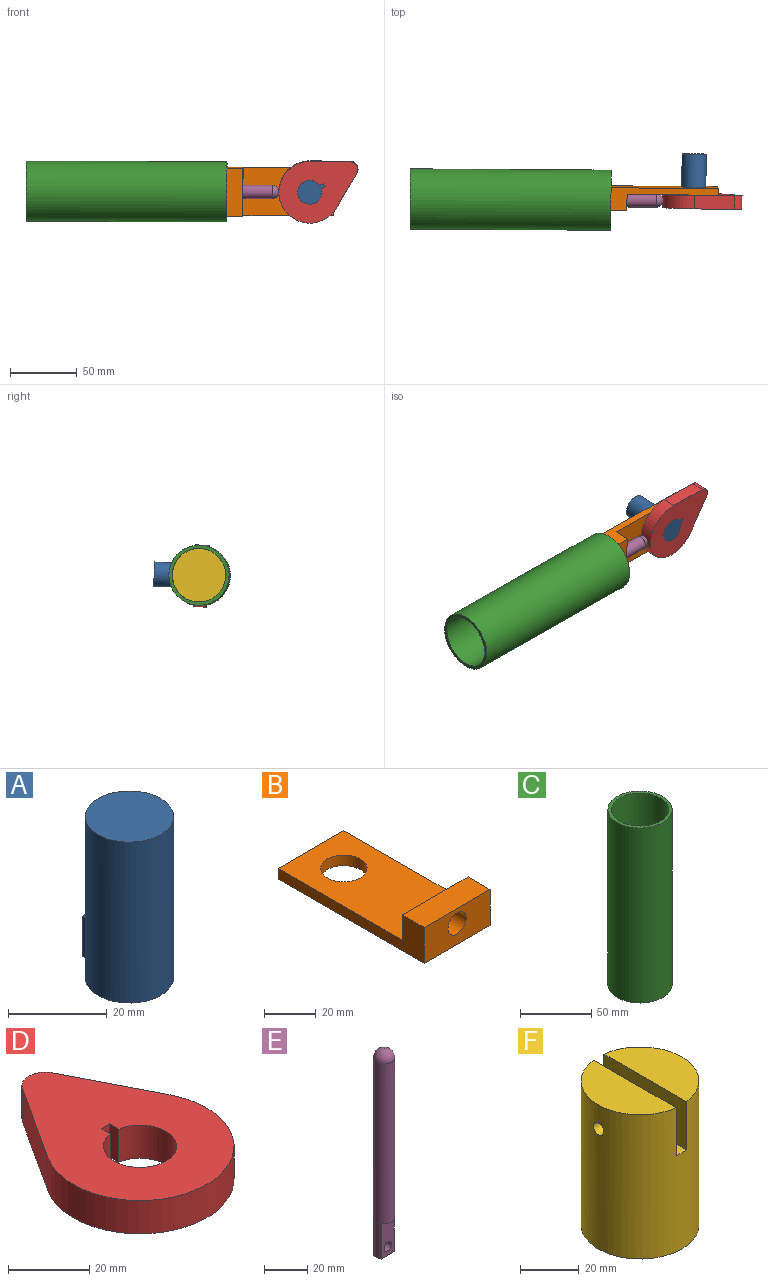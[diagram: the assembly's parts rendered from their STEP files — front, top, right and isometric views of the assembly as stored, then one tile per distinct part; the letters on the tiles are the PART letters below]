
ASSEMBLY  parts=6 mates=7
PART A: 7 faces, bbox 18x21x40 mm
  f0: plane 10x3.13mm, normal (-1,0,0), area 31.3mm2, adj f2,f4,f5,f6
  f1: plane 10x3.13mm, normal (1,0,0), area 31.3mm2, adj f2,f4,f5,f6
  f2: plane 10x3mm, normal (0,1,0), area 30mm2, adj f0,f1,f5,f6
  f3: plane 18x18mm, normal (0,0,1), area 254.5mm2, adj f4
  f4: cylinder r=9mm len=40mm, axis (0,0,-1), area 2231.8mm2, adj f0,f1,f3,f5,f6
  f5: plane 21x18mm, normal (0,0,-1), area 263.6mm2, adj f0,f1,f2,f4
  f6: plane 3.13x3mm, normal (0,0,1), area 9.1mm2, adj f0,f1,f2,f4
PART B: 10 faces, bbox 36x80x17 mm
  f0: plane 68x36mm, normal (0,0,1), area 2193.5mm2, adj f1,f3,f4,f5,f7
  f1: plane 80x17mm, normal (-1,0,0), area 544mm2, adj f0,f2,f4,f6,f7,f8
  f2: plane 36x17mm, normal (0,-1,0), area 533.5mm2, adj f1,f3,f6,f8,f9
  f3: plane 80x17mm, normal (1,0,0), area 544mm2, adj f0,f2,f4,f6,f7,f8
  f4: plane 36x5mm, normal (0,1,0), area 180mm2, adj f0,f1,f3,f6
  f5: cylinder r=9mm len=18mm, axis (0,0,-1), area 282.7mm2, adj f0,f6
  f6: plane 80x36mm, normal (0,0,-1), area 2625.5mm2, adj f1,f2,f3,f4,f5
  f7: plane 36x12mm, normal (0,1,0), area 353.5mm2, adj f0,f1,f3,f8,f9
  f8: plane 36x12mm, normal (0,0,1), area 432mm2, adj f1,f2,f3,f7
  f9: cylinder r=5mm len=12mm, axis (0,1,0), area 377mm2, adj f2,f7
PART C: 4 faces, bbox 45x45x150 mm
  f0: cylinder r=20mm len=150mm, axis (0,0,-1), area 18849.6mm2, adj f2,f3
  f1: cylinder r=22.5mm len=150mm, axis (0,0,-1), area 21205.8mm2, adj f2,f3
  f2: plane 45x45mm, normal (0,0,1), area 333.8mm2, adj f0,f1
  f3: plane 45x45mm, normal (0,0,-1), area 333.8mm2, adj f0,f1
PART D: 10 faces, bbox 46.2x63.5x10 mm
  f0: cylinder r=9mm len=18mm, axis (0,0,-1), area 535.3mm2, adj f1,f2,f7,f9
  f1: plane 63.48x46.2mm, normal (0,0,1), area 1755.7mm2, adj f0,f3,f4,f5,f6,f7,f8,f9
  f2: plane 63.48x46.2mm, normal (0,0,-1), area 1755.7mm2, adj f0,f3,f4,f5,f6,f7,f8,f9
  f3: cylinder r=5.78mm len=10mm, axis (0,0,-1), area 121.1mm2, adj f1,f2,f4,f6
  f4: plane 25.16x16.33mm, normal (-0.84,0.54,0), area 300mm2, adj f1,f2,f3,f5
  f5: cylinder r=23.1mm len=46.2mm, axis (0,0,-1), area 967.7mm2, adj f1,f2,f4,f6
  f6: plane 26.73x13.63mm, normal (0.89,0.45,0), area 300mm2, adj f1,f2,f3,f5
  f7: plane 10x3.13mm, normal (-1,0,0), area 31.3mm2, adj f0,f1,f2,f8
  f8: plane 10x3mm, normal (0,-1,0), area 30mm2, adj f1,f2,f7,f9
  f9: plane 10x3.13mm, normal (1,0,0), area 31.3mm2, adj f0,f1,f2,f8
PART E: 8 faces, bbox 10x10x115 mm
  f0: plane 10x5mm, normal (0,0,-1), area 47.8mm2, adj f1,f3,f5
  f1: cylinder r=5mm len=110mm, axis (0,0,-1), area 3036.9mm2, adj f0,f2,f3,f4,f5,f6
  f2: sphere r=5mm, area 157.1mm2, adj f1
  f3: plane 20x8.66mm, normal (0,1,0), area 153.6mm2, adj f0,f1,f4,f7
  f4: plane 8.66x2.5mm, normal (0,0,-1), area 15.4mm2, adj f1,f3
  f5: plane 20x8.66mm, normal (0,-1,0), area 153.6mm2, adj f0,f1,f6,f7
  f6: plane 8.66x2.5mm, normal (0,0,-1), area 15.4mm2, adj f1,f5
  f7: cylinder r=2.5mm len=5mm, axis (0,-1,0), area 78.5mm2, adj f3,f5
PART F: 9 faces, bbox 40x40x60 mm
  f0: cylinder r=20mm len=60mm, axis (0,0,-1), area 7300mm2, adj f1,f2,f3,f4,f5,f6,f7,f8
  f1: plane 39.69x17.5mm, normal (0,0,1), area 528.6mm2, adj f0,f4
  f2: plane 39.69x17.5mm, normal (0,0,1), area 528.6mm2, adj f0,f5
  f3: plane 40x40mm, normal (0,0,-1), area 1256.6mm2, adj f0
  f4: plane 39.69x20mm, normal (-1,0,0), area 774.1mm2, adj f0,f1,f6,f8
  f5: plane 39.69x20mm, normal (1,0,0), area 774.1mm2, adj f0,f2,f6,f7
  f6: plane 40x5mm, normal (0,0,1), area 199.5mm2, adj f0,f4,f5
  f7: cylinder r=2.5mm len=17.5mm, axis (1,0,0), area 273.7mm2, adj f0,f5
  f8: cylinder r=2.5mm len=17.5mm, axis (1,0,0), area 273.7mm2, adj f0,f4
PLACE A rot(axis=(-0.4,-0.63,-0.66),135.4deg) t=(44.31,54.3,-5.93)mm
PLACE B rot(axis=(0.59,0.58,-0.56),121.7deg) t=(26.37,63.1,147.02)mm fixed
PLACE C rot(axis=(-0.71,0.02,-0.71),178.5deg) t=(-168.55,236.72,69.81)mm
PLACE D rot(axis=(-0.4,-0.63,-0.66),135.4deg) t=(48.7,50.48,82.87)mm
PLACE E rot(axis=(-0.71,0.02,-0.71),178.5deg) t=(-95.94,49.75,24.86)mm
PLACE F rot(axis=(-0.57,0.6,-0.57),118.9deg) t=(-140.1,116.6,173.44)mm
MATE revolute F.f7 <-> E.f7  axis (-0.01,-1,-0.04) through (-90.82,60.73,44.36)mm
MATE planar C.f0 <-> B.f2  axis (1,-0.01,0) through (-19.73,57.79,44.05)mm
MATE slider E.f1 <-> B.f9  axis (-1,0.01,0) through (-95.83,58.26,44.27)mm
MATE planar A.f4 <-> D.f0  axis (-0.01,-1,-0.04) through (42.23,52.19,43.65)mm
MATE slider A.f4 <-> D.f0  axis (-0.01,-1,-0.04) through (42.23,52.19,43.65)mm
MATE cylindrical B.f5 <-> A.f4  axis (-0.01,-1,-0.04) through (42.3,62.4,44.09)mm
MATE slider C.f0 <-> F.f0  axis (-1,0.01,0) through (-169.73,58.72,44.48)mm
